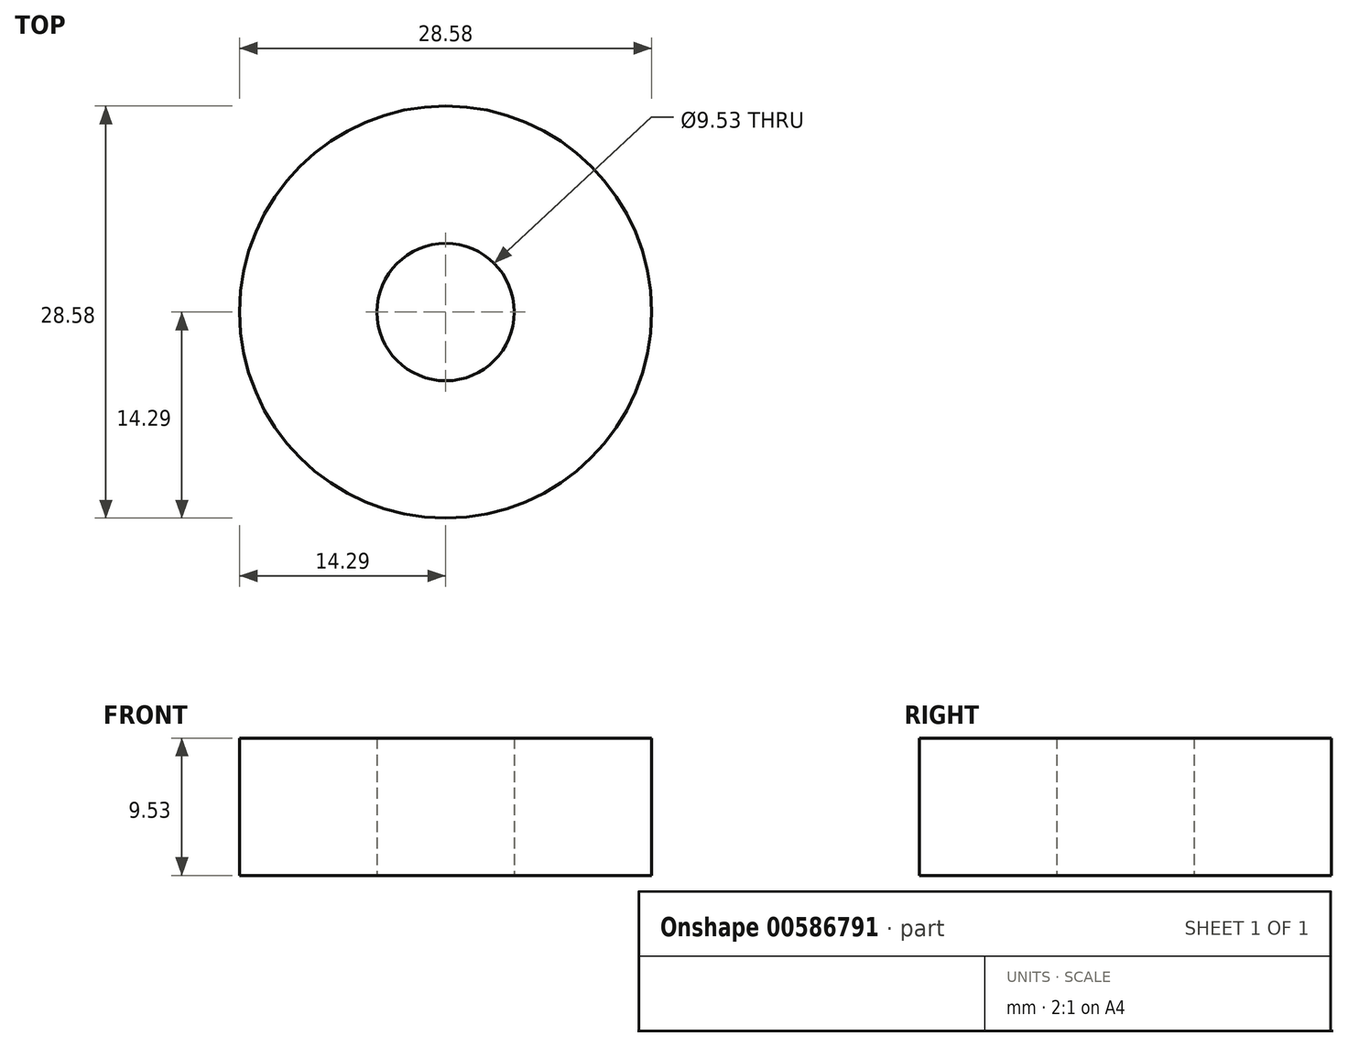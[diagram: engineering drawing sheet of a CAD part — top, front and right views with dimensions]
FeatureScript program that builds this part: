
annotation { "Feature Type Name" : "Feature", "Feature Type Description" : "" }
export const myFeature = defineFeature(function(context is Context, id is Id, definition is map)
    precondition{}
    {
        {
            var Q0;
            Q0=qCreatedBy(makeId("Top.planeOp"),FACE);
            var sketch = newSketch(context, id + "F0", { "sketchPlane" : qUnion([Q0])});
            skCircle(sketch, "E0", {"center": v(0, 0) * mm, "radius": 4.76 * mm});
            skCircle(sketch, "E1", {"center": v(0, 0) * mm, "radius": 14.29 * mm});
            skSolve(sketch);
        }
        {
            var Q0;
            Q0 = qSketchRegion(id + "F0", true);
            extrude(context, id + "F1", {"entities" : qUnion([Q0]), "depth" : 9.52 * mm, "offsetDistance" : 25.4 * mm});
        }
    });
